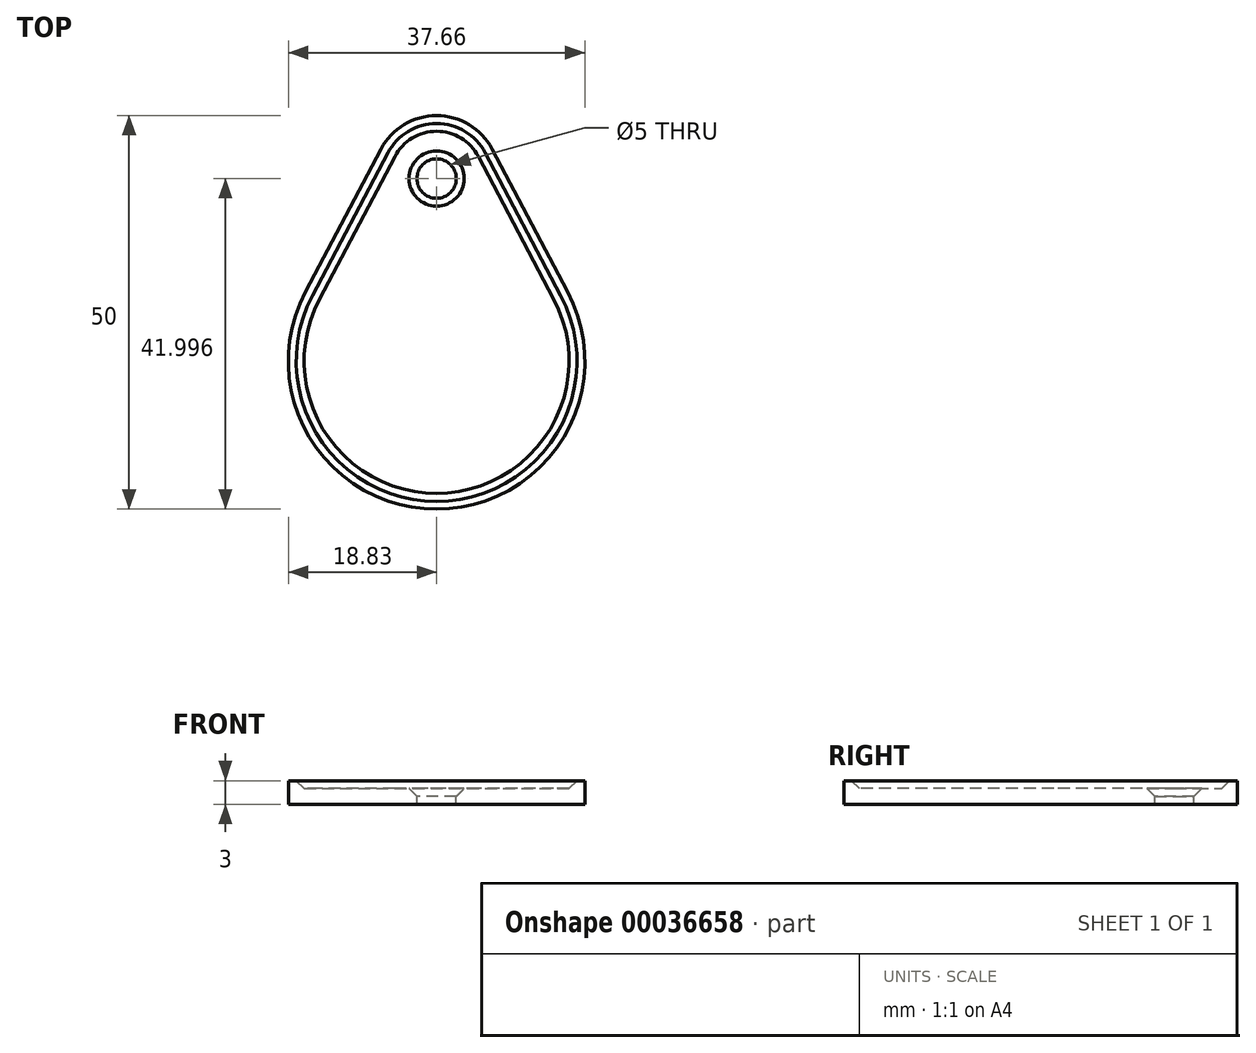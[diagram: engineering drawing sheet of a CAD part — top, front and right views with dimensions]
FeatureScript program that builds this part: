
annotation { "Feature Type Name" : "Feature", "Feature Type Description" : "" }
export const myFeature = defineFeature(function(context is Context, id is Id, definition is map)
    precondition{}
    {
        {
            var Q0;
            Q0=qCreatedBy(makeId("Top.planeOp"),FACE);
            var sketch = newSketch(context, id + "F0", { "sketchPlane" : qUnion([Q0])});
            skLineSegment(sketch, "E0", {"start": v(-16.65, 0) * mm, "end": v(-7.07, 18.1) * mm});
            skLineSegment(sketch, "E1", {"start": v(7.07, 18.1) * mm, "end": v(16.65, 0) * mm});
            skPoint(sketch, "E2.visualSharp", {"position": v(0, 31.48) * mm});
            skArc(sketch, "E2.filletArc", {"start": v(7.07, 18.1) * mm, "mid": v(0, 22.37) * mm, "end": v(-7.07, 18.1) * mm});
            skArc(sketch, "E3", {"start": v(-16.65, 0) * mm, "mid": v(0, -27.63) * mm, "end": v(16.65, 0) * mm});
            skSolve(sketch);
        }
        {
            var Q0;
            Q0 = qSketchRegion(id + "F0", true);
            extrude(context, id + "F1", {"entities" : qUnion([Q0]), "depth" : 3 * mm});
        }
        {
            var Q0;
            Q0=makeQuery(id+"F1.opExtrude","CAP_FACE",FACE,{"disambiguationData":[OSD([sQuery(id+"F0.wireOp",EDGE,"E0"),sQuery(id+"F0.wireOp",EDGE,"E1"),sQuery(id+"F0.wireOp",EDGE,"1d8a8107-0fa0-4a97-bcfc-8f889be78b06"),sQuery(id+"F0.wireOp",EDGE,"db75257c-d4cc-43fa-abbd-30e3bfb7ee45"),sQuery(id+"F0.wireOp",EDGE,"aac4547d-11b7-4ba3-90db-40d1beb6f638"),sQuery(id+"F0.wireOp",EDGE,"E2.filletArc")])],"isStart":false});
            var sketch = newSketch(context, id + "F2", { "sketchPlane" : qUnion([Q0])});
            skCircle(sketch, "E4", {"center": v(0, 14.37) * mm, "radius": 2.5 * mm});
            skSolve(sketch);
        }
        {
            var Q0;
            Q0 = qSketchRegion(id + "F2", true);
            extrude(context, id + "F3", {"entities" : qUnion([Q0]), "operationType" : NewBodyOperationType.REMOVE, "oppositeDirection" : true, "depth" : 25 * mm});
        }
        {
            var Q0;
            Q0=makeQuery(id+"F1.opExtrude","CAP_FACE",FACE,{"disambiguationData":[OSD([sQuery(id+"F0.wireOp",EDGE,"E0"),sQuery(id+"F0.wireOp",EDGE,"E1"),sQuery(id+"F0.wireOp",EDGE,"1d8a8107-0fa0-4a97-bcfc-8f889be78b06"),sQuery(id+"F0.wireOp",EDGE,"db75257c-d4cc-43fa-abbd-30e3bfb7ee45"),sQuery(id+"F0.wireOp",EDGE,"aac4547d-11b7-4ba3-90db-40d1beb6f638"),sQuery(id+"F0.wireOp",EDGE,"E2.filletArc")])],"isStart":false});
            var sketch = newSketch(context, id + "F4", { "sketchPlane" : qUnion([Q0])});
            skLineSegment(sketch, "E5.0", {"start": v(6.19, 17.64) * mm, "end": v(15.76, -0.47) * mm});
            skArc(sketch, "E5.1", {"start": v(6.19, 17.64) * mm, "mid": v(0, 21.37) * mm, "end": v(-6.19, 17.64) * mm});
            skLineSegment(sketch, "E5.2", {"start": v(-15.76, -0.47) * mm, "end": v(-6.19, 17.64) * mm});
            skArc(sketch, "E5.3", {"start": v(-15.76, -0.47) * mm, "mid": v(0, -26.63) * mm, "end": v(15.76, -0.47) * mm});
            skSolve(sketch);
        }
        {
            var Q0;
            Q0 = qSketchRegion(id + "F4", true);
            extrude(context, id + "F5", {"entities" : qUnion([Q0]), "operationType" : NewBodyOperationType.REMOVE, "oppositeDirection" : true, "depth" : 1 * mm});
        }
        {
            var Q0;
            Q0=makeQuery(id+"F5.boolean.opBoolean","COPY",FACE,{"derivedFrom":makeQuery(id+"F5.opExtrude","CAP_FACE",FACE,{"disambiguationData":[OSD([sQuery(id+"F4.wireOp",EDGE,"E5.0"),sQuery(id+"F4.wireOp",EDGE,"E5.1"),sQuery(id+"F4.wireOp",EDGE,"E5.2"),sQuery(id+"F4.wireOp",EDGE,"E5.3")])],"isStart":false})});
            chamfer(context, id + "F6", {"entities" : qUnion([Q0]), "width" : 1 * mm, "tangentPropagation" : true});
        }
    });
